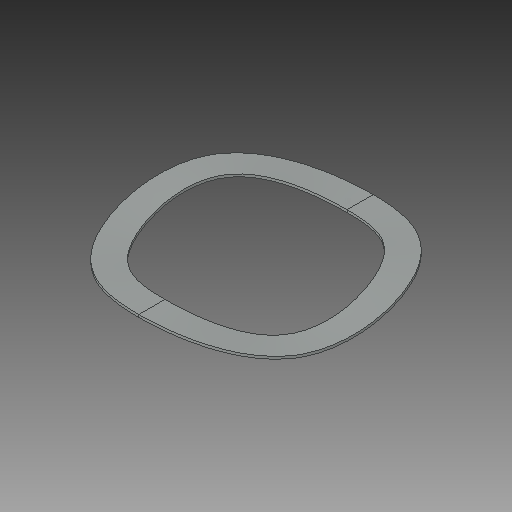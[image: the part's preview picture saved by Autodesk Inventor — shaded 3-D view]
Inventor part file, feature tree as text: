
AUTODESK INVENTOR PART (.ipt)
format: ipt  version: 2017 (Build 210142000, 142)  size: 122,880 bytes
history: native  units: in
note: dims shown in document units (in); Inventor stores cm internally (conversion verified against a paired STEP export)
features: loft x1
ambient origin geometry x8: Origin, YZ Plane, XZ Plane, XY Plane, X Axis, Y Axis, Z Axis, Center Point
bodies: Solid1 (feature_tree)
feature tree (1):
  loft  "Loft1"
